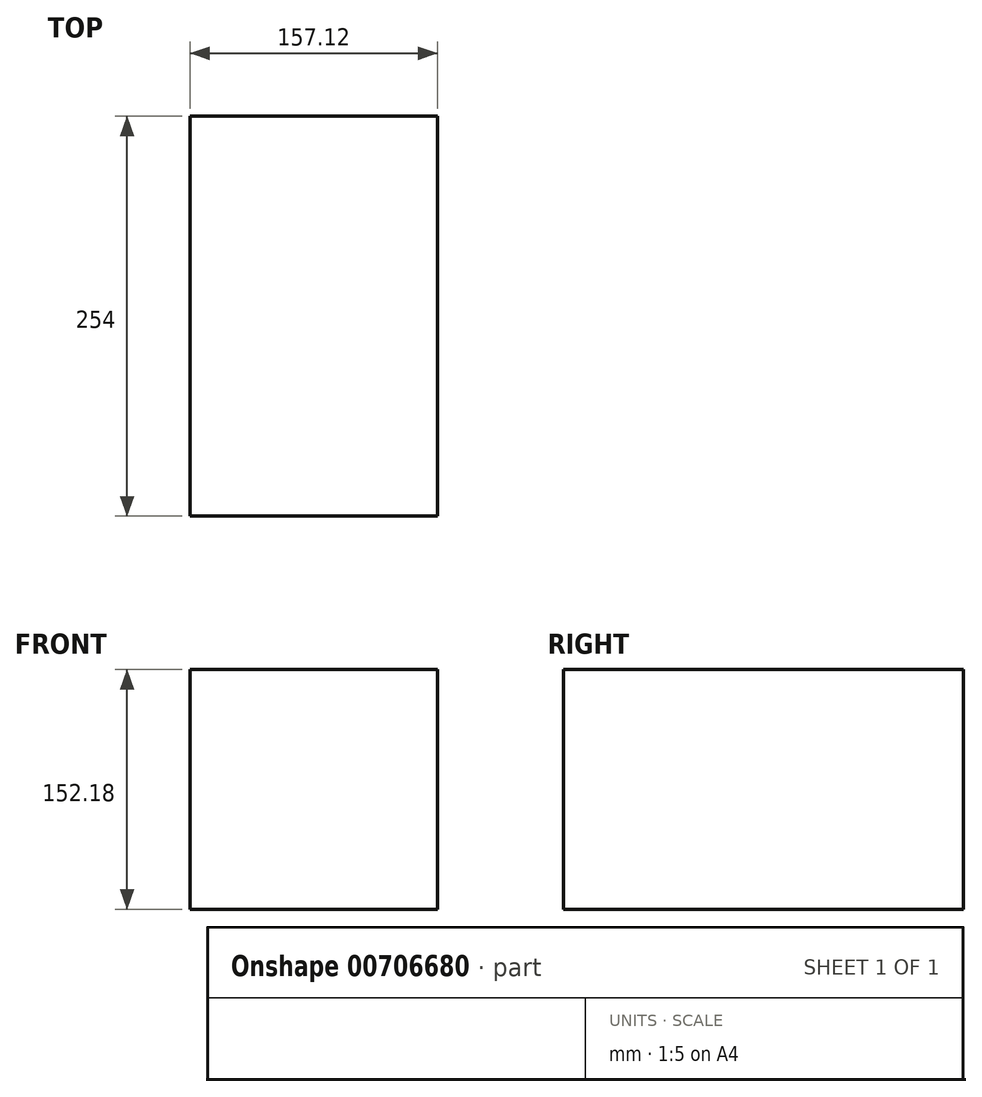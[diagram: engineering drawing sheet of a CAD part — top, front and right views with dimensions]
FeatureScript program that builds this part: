
annotation { "Feature Type Name" : "Feature", "Feature Type Description" : "" }
export const myFeature = defineFeature(function(context is Context, id is Id, definition is map)
    precondition{}
    {
        {
            var Q0;
            Q0=qCreatedBy(makeId("Front.planeOp"),FACE);
            var sketch = newSketch(context, id + "F0", { "sketchPlane" : qUnion([Q0])});
            skLineSegment(sketch, "E0.bottom", {"start": v(-78.56, 76.1) * mm, "end": v(78.56, 76.1) * mm});
            skLineSegment(sketch, "E0.top", {"start": v(-78.56, -76.1) * mm, "end": v(78.56, -76.1) * mm});
            skLineSegment(sketch, "E0.left", {"start": v(-78.56, 76.1) * mm, "end": v(-78.56, -76.1) * mm});
            skLineSegment(sketch, "E0.right", {"start": v(78.56, 76.1) * mm, "end": v(78.56, -76.1) * mm});
            skPoint(sketch, "E0.middle", {"position": v(0, 0) * mm});
            skSolve(sketch);
        }
        {
            var Q0;
            Q0=makeQuery(id+"F0.imprint","IMPRINT",FACE,{"disambiguationData":[TD([[makeQuery(id+"F0.imprint","IMPRINT",EDGE,{"derivedFrom":sQuery(id+"F0.wireOp",EDGE,"E0.bottom")}),-1.0]])]});
            extrude(context, id + "F1", {"entities" : qUnion([Q0]), "depth" : 254 * mm, "offsetDistance" : 25.4 * mm});
        }
    });
